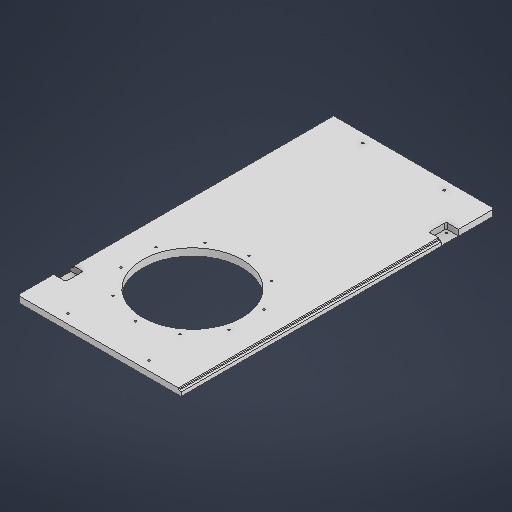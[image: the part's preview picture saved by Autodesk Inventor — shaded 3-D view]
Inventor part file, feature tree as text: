
AUTODESK INVENTOR PART (.ipt)
format: ipt  version: 2025 (Build 290162000, 162)  size: 332,288 bytes
history: native  units: in
note: dims shown in document units (in); Inventor stores cm internally (conversion verified against a paired STEP export)
features: sketch x9, chamfer x5, extrude x4, hole x3, plane x2, fillet x1
ambient origin geometry x8: Origin, YZ Plane, XZ Plane, XY Plane, X Axis, Y Axis, Z Axis, Center Point
bodies: Solid1 (feature_tree)
feature tree (24):
  extrude  "Extrusion1"  Depth=27.1654in
  sketch  "Sketch2"  dims[d2=0.625in d3=0.0in d4=8.0709in]
  extrude  "Extrusion2"  Depth=0.625in
  plane  "Work Plane1"
  hole  "Hole3"  [1 undecoded]
  sketch  "Sketch7"  dims[d56=25.5906in]
  plane  "Work Plane2"
  hole  "Hole4"  [1 undecoded]
  sketch  "Sketch9"  dims[d64=10.3543in]
  fillet  "Fillet2"  Radius=7.0625in
  chamfer  "Chamfer1"  Distance=1.063in
  chamfer  "Chamfer2"  Distance=1.063in
  extrude  "Extrusion7"  Depth=1.4961in
  extrude  "Extrusion8"  Depth=1.4961in
  chamfer  "Chamfer3"  Distance=3.1102in
  chamfer  "Chamfer4"  Distance=3.1102in
  hole  "Hole5"  [1 undecoded]
  chamfer  "Chamfer5"  Distance=0.0984in Angle=45.0deg
  sketch  "Sketch1"  dims[d0=14.1732in d1=27.1654in]
  sketch  "Sketch6"  dims[d8=10.6299in d50=5.9055in d55=7.0625in]
  sketch  "Sketch8"  dims[d57=0.1936in d58=0.1969in d59=0.1575in d60=0.0787in d61=90.0deg d62=0.1969in d63=0.8108in]
  sketch  "Sketch10"  dims[d65=10.6299in]
  sketch  "Sketch11"  dims[d68=9.8425in d74=0.1628in d75=0.3937in d76=0.1575in d77=0.0787in d78=90.0deg d79=0.3937in d80=0.8108in d82=1.063in d83=1.063in d84=1.4961in d85=1.4961in d86=3.1102in d87=3.1102in d88=0.1969in d89=0.0984in d90=0.0787in d91=45.0deg d92=0.0984in d93=0.0787in d94=45.0deg d95=0.1181in d96=0.1181in d97=0.4951in d98=0.0in d99=0.2362in d100=0.2362in d101=0.122in d102=0.0in d103=0.0787in d104=0.1378in d105=45.0deg d106=0.1378in d107=0.0787in d108=45.0deg d109=0.748in d110=0.315in d111=0.8661in d112=0.748in d113=0.1299in d114=0.1299in d115=0.1299in d116=0.1299in d118=0.315in d119=0.8661in d120=0.748in d121=0.748in d122=0.1276in d123=0.315in d124=0.1575in d125=0.0787in d126=90.0deg d127=0.315in d128=0.8108in d129=0.0138in d130=0.0787in d131=45.0deg d146=0.1969in d147=3.937in d149=360.0deg d26=0.0394in d27=0.0394in d28=0.0394in d29=0.0059in d30=0.0098in d31=0.0148in d32=0.5635in d33=0.0295in d34=0.8108in d35=0.0025in d36=0.0295in d37=0.0148in d66=0.0197in d67=0.0344in]
  sketch  "Sketch Circular Pattern5"  dims[d5=8.6614in d6=0.0in d7=0.0in]
note: 3 required parameter values undecoded (feature->parameter linkage not recoverable at this tier; creation-order binding heuristic only, values carry confidence <= 0.55)
